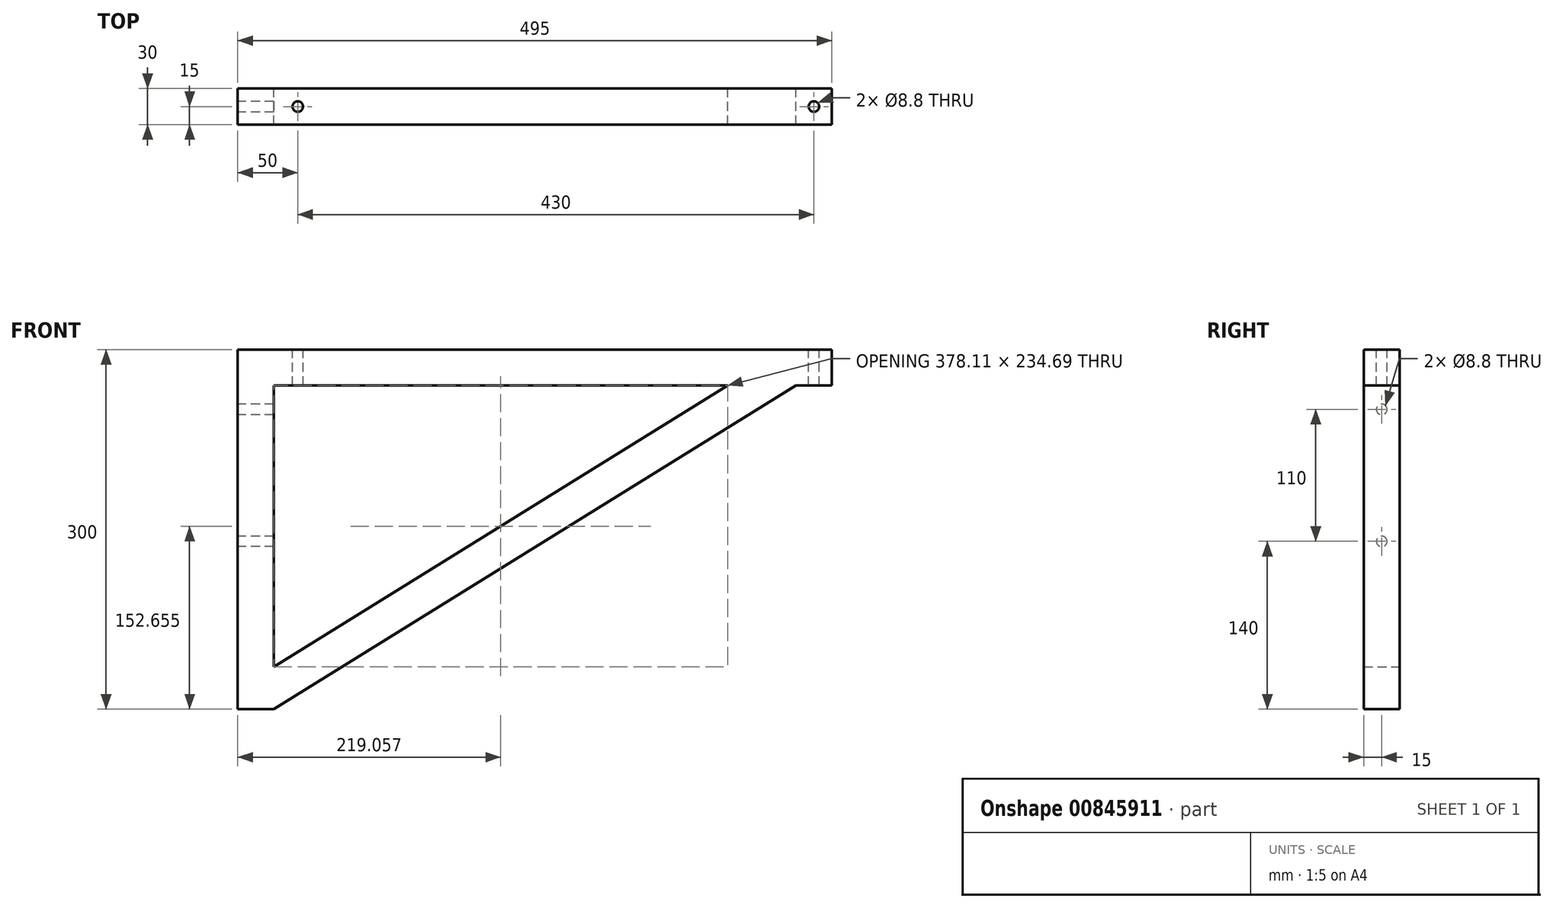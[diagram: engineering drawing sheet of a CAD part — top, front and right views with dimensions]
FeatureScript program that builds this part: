
annotation { "Feature Type Name" : "Feature", "Feature Type Description" : "" }
export const myFeature = defineFeature(function(context is Context, id is Id, definition is map)
    precondition{}
    {
        {
            var Q0;
            Q0=qCreatedBy(makeId("Front.planeOp"),FACE);
            var sketch = newSketch(context, id + "F0", { "sketchPlane" : qUnion([Q0])});
            skLineSegment(sketch, "E0", {"start": v(0, 0) * mm, "end": v(495, 0) * mm});
            skLineSegment(sketch, "E1", {"start": v(0, 0) * mm, "end": v(0, -300) * mm});
            skLineSegment(sketch, "E2", {"start": v(0, -300) * mm, "end": v(30, -300) * mm});
            skLineSegment(sketch, "E3", {"start": v(30, -300) * mm, "end": v(30, -300) * mm});
            skLineSegment(sketch, "E4", {"start": v(30, -30) * mm, "end": v(408.11, -30) * mm});
            skLineSegment(sketch, "E5", {"start": v(465, -30) * mm, "end": v(30, -300) * mm});
            skLineSegment(sketch, "E6", {"start": v(408.11, -30) * mm, "end": v(30, -264.7) * mm});
            skLineSegment(sketch, "E7.trimOffspring", {"start": v(30, -264.7) * mm, "end": v(30, -30) * mm});
            skLineSegment(sketch, "E8", {"start": v(495, 0) * mm, "end": v(495, -30) * mm});
            skLineSegment(sketch, "E9", {"start": v(495, -30) * mm, "end": v(465, -30) * mm});
            skSolve(sketch);
        }
        {
            var Q0;
            Q0=makeQuery(id+"F0.imprint","IMPRINT",FACE,{"disambiguationData":[TD([[makeQuery(id+"F0.imprint","IMPRINT",EDGE,{"derivedFrom":sQuery(id+"F0.wireOp",EDGE,"E0")}),-1.0]])]});
            extrude(context, id + "F1", {"entities" : qUnion([Q0]), "depth" : 30 * mm, "offsetDistance" : 25 * mm});
        }
        {
            var Q0;
            Q0=makeQuery(id+"F1.opExtrude","SWEPT_FACE",FACE,{"disambiguationData":[OSD([sQuery(id+"F0.wireOp",EDGE,"E1")])]});
            var sketch = newSketch(context, id + "F2", { "sketchPlane" : qUnion([Q0])});
            skPoint(sketch, "E10", {"position": v(15, -50) * mm});
            skPoint(sketch, "E11", {"position": v(15, -160) * mm});
            skSolve(sketch);
        }
        {
            var Q0;
            Q0=sQuery(id+"F2.wireOp",VERTEX,"E10");
            var Q1;
            Q1=sQuery(id+"F2.wireOp",VERTEX,"E11");
            var Q2;
            Q2=makeQuery(id+"F1.opExtrude","SWEPT_BODY",BODY,{"disambiguationData":[OSD([sQuery(id+"F0.wireOp",EDGE,"E0"),sQuery(id+"F0.wireOp",EDGE,"E1"),sQuery(id+"F0.wireOp",EDGE,"E2"),sQuery(id+"F0.wireOp",EDGE,"E4"),sQuery(id+"F0.wireOp",EDGE,"E5"),sQuery(id+"F0.wireOp",EDGE,"E6"),sQuery(id+"F0.wireOp",EDGE,"E7.trimOffspring"),sQuery(id+"F0.wireOp",EDGE,"E8"),sQuery(id+"F0.wireOp",EDGE,"E9")])]});
            hole(context, id + "F3", {"style" : HoleStyle.SIMPLE, "endStyle" : HoleEndStyle.BLIND, "standardTappedOrClearance" : lookupTablePath({ "fit" : "Normal", "standard" : "ISO", "size" : "M8", "type" : "Clearance" }), "standardBlindInLast" : lookupTablePath({ "fit" : "Standard", "standard" : "ISO", "size" : "M8", "type" : "Clearance" }), "holeDiameter" : 8.8 * mm, "majorDiameter" : 5 * mm, "holeDepth" : 30 * mm, "isTappedThrough" : true, "tappedDepth" : 26.25 * mm, "tapClearance" : 3, "locations" : qUnion([Q0, Q1]), "scope" : qUnion([Q2])});
        }
        {
            var Q0;
            Q0=makeQuery(id+"F1.opExtrude","SWEPT_FACE",FACE,{"disambiguationData":[OSD([sQuery(id+"F0.wireOp",EDGE,"E0")])]});
            var sketch = newSketch(context, id + "F4", { "sketchPlane" : qUnion([Q0])});
            skPoint(sketch, "E12", {"position": v(480, -15) * mm});
            skPoint(sketch, "E12.positionSnap0", {"position": v(495, -15) * mm});
            skPoint(sketch, "E13", {"position": v(50, -15) * mm});
            skSolve(sketch);
        }
        {
            var Q0;
            Q0=sQuery(id+"F4.wireOp",VERTEX,"E12");
            var Q1;
            Q1=sQuery(id+"F4.wireOp",VERTEX,"E13");
            var Q2;
            Q2=makeQuery(id+"F1.opExtrude","SWEPT_BODY",BODY,{"disambiguationData":[OSD([sQuery(id+"F0.wireOp",EDGE,"E0"),sQuery(id+"F0.wireOp",EDGE,"E1"),sQuery(id+"F0.wireOp",EDGE,"E2"),sQuery(id+"F0.wireOp",EDGE,"E4"),sQuery(id+"F0.wireOp",EDGE,"E5"),sQuery(id+"F0.wireOp",EDGE,"E6"),sQuery(id+"F0.wireOp",EDGE,"E7.trimOffspring"),sQuery(id+"F0.wireOp",EDGE,"E8"),sQuery(id+"F0.wireOp",EDGE,"E9")])]});
            hole(context, id + "F5", {"style" : HoleStyle.SIMPLE, "endStyle" : HoleEndStyle.BLIND, "standardTappedOrClearance" : lookupTablePath({ "fit" : "Normal", "standard" : "ISO", "size" : "M8", "type" : "Clearance" }), "standardBlindInLast" : lookupTablePath({ "fit" : "Standard", "standard" : "ISO", "size" : "M8", "type" : "Clearance" }), "holeDiameter" : 8.8 * mm, "majorDiameter" : 5 * mm, "holeDepth" : 30 * mm, "isTappedThrough" : true, "tappedDepth" : 26.25 * mm, "tapClearance" : 3, "locations" : qUnion([Q0, Q1]), "scope" : qUnion([Q2])});
        }
    });
